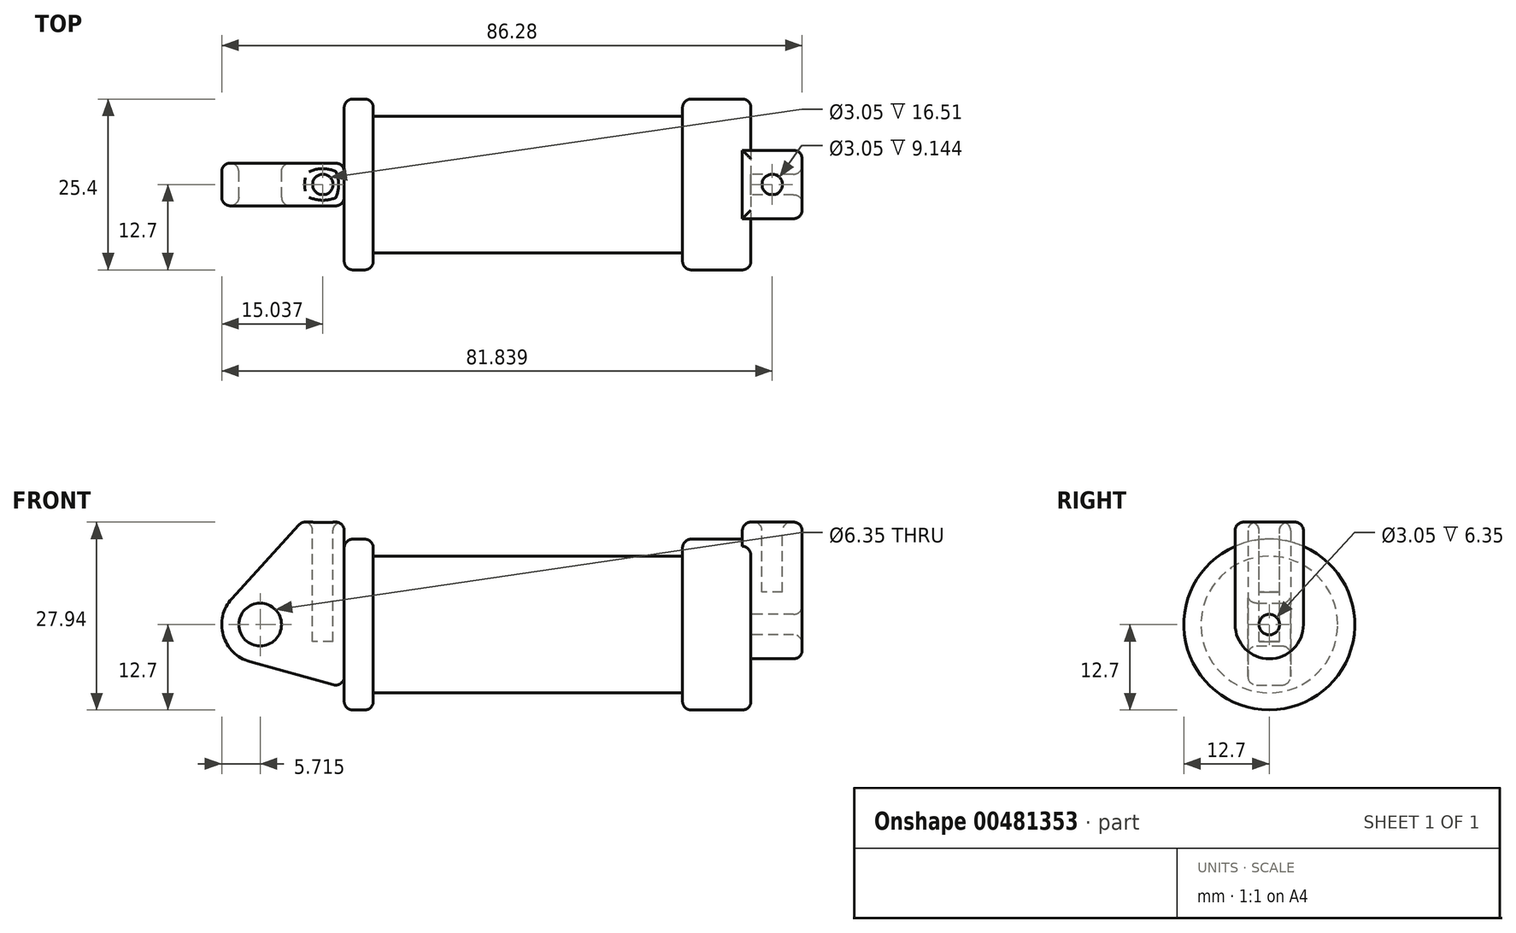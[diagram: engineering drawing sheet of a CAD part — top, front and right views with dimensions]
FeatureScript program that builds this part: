
annotation { "Feature Type Name" : "Feature", "Feature Type Description" : "" }
export const myFeature = defineFeature(function(context is Context, id is Id, definition is map)
    precondition{}
    {
        {
            var Q0;
            Q0=qCreatedBy(makeId("Front.planeOp"),FACE);
            var sketch = newSketch(context, id + "F0", { "sketchPlane" : qUnion([Q0])});
            skLineSegment(sketch, "E0", {"start": v(0, 0) * mm, "end": v(0, 12.7) * mm});
            skLineSegment(sketch, "E1", {"start": v(0, 12.7) * mm, "end": v(10.16, 12.7) * mm});
            skLineSegment(sketch, "E2", {"start": v(10.16, 12.7) * mm, "end": v(10.16, 10.16) * mm});
            skLineSegment(sketch, "E3", {"start": v(10.16, 10.16) * mm, "end": v(56.13, 10.16) * mm});
            skLineSegment(sketch, "E4", {"start": v(56.13, 10.16) * mm, "end": v(56.13, 12.7) * mm});
            skLineSegment(sketch, "E5", {"start": v(56.13, 12.7) * mm, "end": v(66.3, 12.7) * mm});
            skLineSegment(sketch, "E6", {"start": v(66.3, 12.7) * mm, "end": v(66.3, 0) * mm});
            skLineSegment(sketch, "E7", {"start": v(66.3, 0) * mm, "end": v(0, 0) * mm});
            skLineSegment(sketch, "E8", {"start": v(5.84, 15.24) * mm, "end": v(-0.5, 15.24) * mm});
            skLineSegment(sketch, "E9", {"start": v(-0.5, 15.24) * mm, "end": v(-10.88, 3.85) * mm});
            skLineSegment(sketch, "E10", {"start": v(0, 0) * mm, "end": v(-6.65, 0) * mm});
            skCircle(sketch, "E11", {"center": v(-6.65, 0) * mm, "radius": 5.72 * mm});
            skCircle(sketch, "E12", {"center": v(-6.65, 0) * mm, "radius": 3.18 * mm});
            skLineSegment(sketch, "E13", {"start": v(5.84, 15.24) * mm, "end": v(5.84, -9.4) * mm});
            skLineSegment(sketch, "E14", {"start": v(5.84, -9.4) * mm, "end": v(-8.18, -5.5) * mm});
            skSolve(sketch);
        }
        {
            var Q0;
            {var subQ0=sQuery(id+"F0.wireOp",EDGE,"E2");Q0=makeQuery(id+"F0.imprint","IMPRINT",FACE,{"disambiguationData":[TD([[makeQuery(id+"F0.imprint","IMPRINT",EDGE,{"derivedFrom":subQ0}),-1.0]])]});}
            var Q1;
            Q1=sQuery(id+"F0.wireOp",EDGE,"E7");
            revolve(context, id + "F1", {"entities" : qUnion([Q0]), "axis" : qUnion([Q1]), "revolveType" : RevolveType.FULL});
        }
        {
            var Q0;
            {var subQ1=sQuery(id+"F0.wireOp",EDGE,"E0");Q0=makeQuery(id+"F0.imprint","IMPRINT",FACE,{"disambiguationData":[TD([[makeQuery(id+"F0.imprint","IMPRINT",EDGE,{"derivedFrom":subQ1}),1.0]])]});}
            var Q1;
            {var subQ5=sQuery(id+"F0.wireOp",EDGE,"E12");Q1=makeQuery(id+"F0.imprint","IMPRINT",FACE,{"disambiguationData":[TD([[makeQuery(id+"F0.imprint","IMPRINT",EDGE,{"derivedFrom":subQ5}),-1.0]])]});}
            var Q2;
            {var subQ0=sQuery(id+"F0.wireOp",EDGE,"E14");Q2=makeQuery(id+"F0.imprint","IMPRINT",FACE,{"disambiguationData":[TD([[makeQuery(id+"F0.imprint","IMPRINT",EDGE,{"derivedFrom":subQ0}),-1.0]])]});}
            var Q3;
            {var subQ0=sQuery(id+"F0.wireOp",EDGE,"E0");Q3=makeQuery(id+"F0.imprint","IMPRINT",FACE,{"disambiguationData":[TD([[makeQuery(id+"F0.imprint","IMPRINT",EDGE,{"derivedFrom":subQ0}),-1.0]])]});}
            extrude(context, id + "F2", {"entities" : qUnion([Q0, Q1, Q2, Q3]), "endBound" : BoundingType.SYMMETRIC, "depth" : 6.35 * mm});
        }
        {
            var Q0;
            Q0=makeQuery(id+"F1.opRevolve","SWEPT_FACE",FACE,{"disambiguationData":[OSD([sQuery(id+"F0.wireOp",EDGE,"E6")])]});
            var sketch = newSketch(context, id + "F3", { "sketchPlane" : qUnion([Q0])});
            skCircle(sketch, "E15", {"center": v(0, 0) * mm, "radius": 1.52 * mm});
            skCircle(sketch, "E16", {"center": v(0, 0) * mm, "radius": 5.08 * mm});
            skLineSegment(sketch, "E17", {"start": v(5.08, 0) * mm, "end": v(5.08, 15.24) * mm});
            skLineSegment(sketch, "E18", {"start": v(-5.08, 0) * mm, "end": v(-5.08, 15.24) * mm});
            skLineSegment(sketch, "E19", {"start": v(-5.08, 15.24) * mm, "end": v(5.08, 15.24) * mm});
            skSolve(sketch);
        }
        {
            var Q0;
            Q0=makeQuery(id+"F3.imprint","IMPRINT",FACE,{"disambiguationData":[TD([[makeQuery(id+"F3.imprint","IMPRINT",EDGE,{"derivedFrom":sQuery(id+"F3.wireOp",EDGE,"E15")}),-1.0]])]});
            var Q1;
            {var subQ0=sQuery(id+"F3.wireOp",EDGE,"E17");var subQ1=sQuery(id+"F3.wireOp",EDGE,"E16");var subQ2=makeQuery(id+"F3.imprint","INTERSECT",VERTEX,{"derivedFrom":[subQ1,subQ0]});Q1=makeQuery(id+"F3.imprint","IMPRINT",FACE,{"disambiguationData":[TD([[makeQuery(id+"F3.imprint","IMPRINT",EDGE,{"disambiguationData":[TD([[subQ2,-1.0]])],"derivedFrom":subQ1}),-1.0]])]});}
            var Q2;
            {var subQ0=sQuery(id+"F3.wireOp",EDGE,"E19");Q2=makeQuery(id+"F3.imprint","IMPRINT",FACE,{"disambiguationData":[TD([[makeQuery(id+"F3.imprint","IMPRINT",EDGE,{"derivedFrom":subQ0}),-1.0]])]});}
            extrude(context, id + "F4", {"entities" : qUnion([Q0, Q1, Q2]), "operationType" : NewBodyOperationType.ADD, "depth" : 7.62 * mm});
        }
        {
            var Q0;
            {var subQ0=sQuery(id+"F3.wireOp",EDGE,"E19");Q0=makeQuery(id+"F3.imprint","IMPRINT",FACE,{"disambiguationData":[TD([[makeQuery(id+"F3.imprint","IMPRINT",EDGE,{"derivedFrom":subQ0}),-1.0]])]});}
            extrude(context, id + "F5", {"entities" : qUnion([Q0]), "operationType" : NewBodyOperationType.ADD, "oppositeDirection" : true, "depth" : 1.27 * mm});
        }
        {
            var Q0;
            Q0=makeQuery(id+"F2.opExtrude","SWEPT_FACE",FACE,{"disambiguationData":[OSD([sQuery(id+"F0.wireOp",EDGE,"E8")])]});
            var sketch = newSketch(context, id + "F6", { "sketchPlane" : qUnion([Q0])});
            skCircle(sketch, "E20", {"center": v(2.67, 0) * mm, "radius": 1.52 * mm});
            skPoint(sketch, "E20.centerSnap0", {"position": v(5.84, 0) * mm});
            skPoint(sketch, "E20.centerSnap1", {"position": v(2.67, 3.18) * mm});
            skSolve(sketch);
        }
        {
            var Q0;
            {var subQ0=sQuery(id+"F3.wireOp",EDGE,"E19");Q0=makeQuery(id+"F5.boolean.opBoolean","MERGE",FACE,{"derivedFrom":[makeQuery(id+"F4.opExtrude","SWEPT_FACE",FACE,{"disambiguationData":[OSD([subQ0])]}),makeQuery(id+"F5.opExtrude","SWEPT_FACE",FACE,{"disambiguationData":[OSD([subQ0])]})]});}
            var sketch = newSketch(context, id + "F7", { "sketchPlane" : qUnion([Q0])});
            skCircle(sketch, "E21", {"center": v(69.47, 0) * mm, "radius": 1.52 * mm});
            skPoint(sketch, "E21.centerSnap0", {"position": v(69.47, 5.08) * mm});
            skPoint(sketch, "E21.centerSnap1", {"position": v(65.02, 0) * mm});
            skSolve(sketch);
        }
        {
            var Q0;
            Q0=makeQuery(id+"F6.imprint","IMPRINT",FACE,{"disambiguationData":[TD([[makeQuery(id+"F6.imprint","IMPRINT",EDGE,{"derivedFrom":sQuery(id+"F6.wireOp",EDGE,"E20")}),1.0]])]});
            extrude(context, id + "F8", {"entities" : qUnion([Q0]), "operationType" : NewBodyOperationType.REMOVE, "oppositeDirection" : true, "depth" : 17.78 * mm, "offsetDistance" : 25.4 * mm});
        }
        {
            var Q0;
            Q0=makeQuery(id+"F7.imprint","IMPRINT",FACE,{"disambiguationData":[TD([[makeQuery(id+"F7.imprint","IMPRINT",EDGE,{"derivedFrom":sQuery(id+"F7.wireOp",EDGE,"E21")}),1.0]])]});
            extrude(context, id + "F9", {"entities" : qUnion([Q0]), "operationType" : NewBodyOperationType.REMOVE, "oppositeDirection" : true, "depth" : 10.4 * mm, "offsetDistance" : 25.4 * mm});
        }
        {
            var Q0;
            Q0=makeQuery(id+"F2.opExtrude","SWEPT_FACE",FACE,{"disambiguationData":[OSD([sQuery(id+"F0.wireOp",EDGE,"E11")])]});
            var Q1;
            Q1=makeQuery(id+"F1.opRevolve","SWEPT_FACE",FACE,{"disambiguationData":[OSD([sQuery(id+"F0.wireOp",EDGE,"E1")])]});
            var Q2;
            Q2=makeQuery(id+"F2.opExtrude","SWEPT_FACE",FACE,{"disambiguationData":[OSD([sQuery(id+"F0.wireOp",EDGE,"E8")])]});
            var Q3;
            Q3=makeQuery(id+"F2.opExtrude","SWEPT_FACE",FACE,{"disambiguationData":[OSD([sQuery(id+"F0.wireOp",EDGE,"E9")])]});
            var Q4;
            Q4=makeQuery(id+"F2.opExtrude","CAP_FACE",FACE,{"disambiguationData":[OSD([sQuery(id+"F0.wireOp",EDGE,"E8"),sQuery(id+"F0.wireOp",EDGE,"E9"),sQuery(id+"F0.wireOp",EDGE,"E11"),sQuery(id+"F0.wireOp",EDGE,"E12"),sQuery(id+"F0.wireOp",EDGE,"E13"),sQuery(id+"F0.wireOp",EDGE,"E14")])],"isStart":true});
            var Q5;
            Q5=makeQuery(id+"F2.opExtrude","SWEPT_FACE",FACE,{"disambiguationData":[OSD([sQuery(id+"F0.wireOp",EDGE,"E14")])]});
            var Q6;
            Q6=makeQuery(id+"F2.opExtrude","CAP_FACE",FACE,{"disambiguationData":[OSD([sQuery(id+"F0.wireOp",EDGE,"E8"),sQuery(id+"F0.wireOp",EDGE,"E9"),sQuery(id+"F0.wireOp",EDGE,"E11"),sQuery(id+"F0.wireOp",EDGE,"E12"),sQuery(id+"F0.wireOp",EDGE,"E13"),sQuery(id+"F0.wireOp",EDGE,"E14")])],"isStart":false});
            var Q7;
            Q7=makeQuery(id+"F8.boolean.opBoolean","INTERSECT",EDGE,{"derivedFrom":[makeQuery(id+"F2.opExtrude","SWEPT_FACE",FACE,{"disambiguationData":[OSD([sQuery(id+"F0.wireOp",EDGE,"E14")])]}),makeQuery(id+"F8.opExtrude","SWEPT_FACE",FACE,{"disambiguationData":[OSD([sQuery(id+"F6.wireOp",EDGE,"E20")])]})]});
            fillet(context, id + "F10", {"entities" : qUnion([Q0, Q1, Q2, Q3, Q4, Q5, Q6, Q7]), "radius" : 1.27 * mm, "tangentPropagation" : true, "allowEdgeOverflow" : false});
        }
        {
            var Q0;
            Q0=makeQuery(id+"F9.boolean.opBoolean","COPY",EDGE,{"derivedFrom":makeQuery(id+"F9.opExtrude","CAP_EDGE",EDGE,{"disambiguationData":[OSD([sQuery(id+"F7.wireOp",EDGE,"E21")])],"isStart":true})});
            var Q1;
            {var subQ0=sQuery(id+"F3.wireOp",EDGE,"E19");Q1=makeQuery(id+"F5.boolean.opBoolean","MERGE",FACE,{"derivedFrom":[makeQuery(id+"F4.opExtrude","SWEPT_FACE",FACE,{"disambiguationData":[OSD([subQ0])]}),makeQuery(id+"F5.opExtrude","SWEPT_FACE",FACE,{"disambiguationData":[OSD([subQ0])]})]});}
            var Q2;
            Q2=makeQuery(id+"F4.opExtrude","CAP_FACE",FACE,{"disambiguationData":[OSD([sQuery(id+"F3.wireOp",EDGE,"E15"),sQuery(id+"F3.wireOp",EDGE,"E16"),sQuery(id+"F3.wireOp",EDGE,"E17"),sQuery(id+"F3.wireOp",EDGE,"E18"),sQuery(id+"F3.wireOp",EDGE,"E19")])],"isStart":false});
            var Q3;
            Q3=makeQuery(id+"F1.opRevolve","SWEPT_EDGE",EDGE,{"disambiguationData":[OSD([sQuery(id+"F0.wireOp",EDGE,"E4"),sQuery(id+"F0.wireOp",EDGE,"E5")])]});
            var Q4;
            {var subQ0=sQuery(id+"F0.wireOp",EDGE,"E5");var subQ1=sQuery(id+"F0.wireOp",EDGE,"E6");Q4=makeQuery(id+"F4.boolean.opBoolean","SPLIT",EDGE,{"disambiguationData":[topologyDisambiguationEdgeConnected([makeQuery(id+"F1.opRevolve","SWEPT_FACE",FACE,{"disambiguationData":[OSD([subQ1])]})])],"derivedFrom":makeQuery(id+"F1.opRevolve","SWEPT_EDGE",EDGE,{"disambiguationData":[OSD([subQ0,subQ1])]})});}
            fillet(context, id + "F11", {"entities" : qUnion([Q0, Q1, Q2, Q3, Q4]), "radius" : 1.27 * mm, "tangentPropagation" : true, "allowEdgeOverflow" : false});
        }
    });
